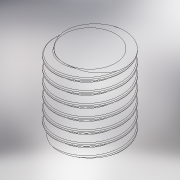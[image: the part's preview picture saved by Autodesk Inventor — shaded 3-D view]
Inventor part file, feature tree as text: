
AUTODESK INVENTOR PART (.ipt)
format: ipt  version: 2019.4 (Build 234330000, 330)  size: 715,264 bytes
history: native  units: mm
features: sketch x2, revolve x1, helix x1, pattern_circular x1
ambient origin geometry x8: Origin, YZ Plane, XZ Plane, XY Plane, X Axis, Y Axis, Z Axis, Center Point
bodies: Solid2 (feature_tree)
feature tree (5):
  revolve  "Revolution1"  [1 undecoded]
  helix  "Coil1"  [1 undecoded]
  pattern_circular  "Circular Pattern1"  [2 undecoded]
  sketch  "Sketch5"  dims[d10=6.992874mm d11=12.5mm d12=10.625mm]
  sketch  "Sketch6"  dims[d14=2.356194mm d15=4.712389mm d16=34.712389mm d17=10.0mm d18=0.0mm d19=90.0deg d20=90.0deg d21=0.0mm d22=0.0mm d23=14.0mm d27=30.0mm d28=90.0deg d29=14.0mm d39=10.0mm d40=360.0deg d42=0.5mm d43=4.712389mm d44=0.5mm d45=0.872665mm d46=0.872665mm d47=10.625mm]
note: 4 required parameter values undecoded (feature->parameter linkage not recoverable at this tier; creation-order binding heuristic only, values carry confidence <= 0.55)